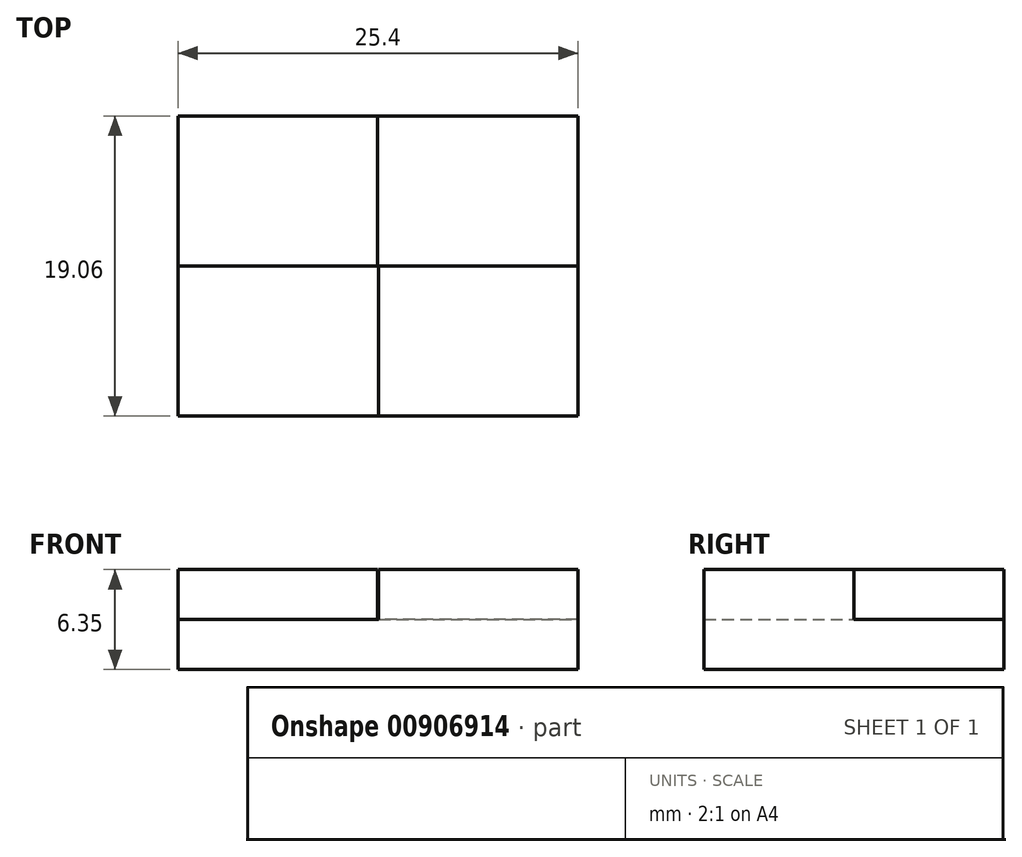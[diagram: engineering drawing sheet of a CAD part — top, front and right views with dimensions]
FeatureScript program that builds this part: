
annotation { "Feature Type Name" : "Feature", "Feature Type Description" : "" }
export const myFeature = defineFeature(function(context is Context, id is Id, definition is map)
    precondition{}
    {
        {
            var Q0;
            Q0=qCreatedBy(makeId("Top.planeOp"),FACE);
            var sketch = newSketch(context, id + "F0", { "sketchPlane" : qUnion([Q0])});
            skLineSegment(sketch, "E0.bottom", {"start": v(12.7, -9.52) * mm, "end": v(-12.7, -9.53) * mm});
            skLineSegment(sketch, "E0.top", {"start": v(12.7, 9.53) * mm, "end": v(-12.7, 9.52) * mm});
            skLineSegment(sketch, "E0.left", {"start": v(12.7, -9.52) * mm, "end": v(12.7, 9.53) * mm});
            skLineSegment(sketch, "E0.right", {"start": v(-12.7, -9.53) * mm, "end": v(-12.7, 9.52) * mm});
            skPoint(sketch, "E0.middle", {"position": v(0, 0) * mm});
            skLineSegment(sketch, "E1", {"start": v(12.7, 0) * mm, "end": v(-12.7, 0) * mm});
            skLineSegment(sketch, "E2", {"start": v(-0.03, 9.53) * mm, "end": v(-0.03, -9.53) * mm});
            skLineSegment(sketch, "E3", {"start": v(0.03, 9.52) * mm, "end": v(0.03, -9.53) * mm});
            skLineSegment(sketch, "E4", {"start": v(0.03, 5.34) * mm, "end": v(0, 5.34) * mm, "construction": true});
            skLineSegment(sketch, "E5", {"start": v(0, 7.47) * mm, "end": v(-0.03, 7.47) * mm, "construction": true});
            skSolve(sketch);
        }
        {
            var Q0;
            {var subQ0=sQuery(id+"F0.wireOp",EDGE,"E0.right");var subQ1=sQuery(id+"F0.wireOp",EDGE,"E0.top");var subQ2=makeQuery(id+"F0.imprint","INTERSECT",VERTEX,{"derivedFrom":[subQ1,subQ0]});Q0=makeQuery(id+"F0.imprint","IMPRINT",FACE,{"disambiguationData":[TD([[makeQuery(id+"F0.imprint","IMPRINT",EDGE,{"disambiguationData":[TD([[subQ2,1.0]])],"derivedFrom":subQ1}),1.0]])]});}
            var Q1;
            {var subQ0=sQuery(id+"F0.wireOp",EDGE,"E0.left");var subQ1=sQuery(id+"F0.wireOp",EDGE,"E0.top");var subQ2=makeQuery(id+"F0.imprint","INTERSECT",VERTEX,{"derivedFrom":[subQ1,subQ0]});Q1=makeQuery(id+"F0.imprint","IMPRINT",FACE,{"disambiguationData":[TD([[makeQuery(id+"F0.imprint","IMPRINT",EDGE,{"disambiguationData":[TD([[subQ2,-1.0]])],"derivedFrom":subQ1}),1.0]])]});}
            var Q2;
            {var subQ0=sQuery(id+"F0.wireOp",EDGE,"E0.left");var subQ1=sQuery(id+"F0.wireOp",EDGE,"E0.bottom");var subQ2=makeQuery(id+"F0.imprint","INTERSECT",VERTEX,{"derivedFrom":[subQ1,subQ0]});Q2=makeQuery(id+"F0.imprint","IMPRINT",FACE,{"disambiguationData":[TD([[makeQuery(id+"F0.imprint","IMPRINT",EDGE,{"disambiguationData":[TD([[subQ2,-1.0]])],"derivedFrom":subQ1}),-1.0]])]});}
            var Q3;
            {var subQ0=sQuery(id+"F0.wireOp",EDGE,"E0.right");var subQ1=sQuery(id+"F0.wireOp",EDGE,"E0.bottom");var subQ2=makeQuery(id+"F0.imprint","INTERSECT",VERTEX,{"derivedFrom":[subQ1,subQ0]});Q3=makeQuery(id+"F0.imprint","IMPRINT",FACE,{"disambiguationData":[TD([[makeQuery(id+"F0.imprint","IMPRINT",EDGE,{"disambiguationData":[TD([[subQ2,1.0]])],"derivedFrom":subQ1}),-1.0]])]});}
            var Q4;
            {var subQ0=sQuery(id+"F0.wireOp",EDGE,"E2");var subQ1=sQuery(id+"F0.wireOp",EDGE,"E0.top");var subQ2=makeQuery(id+"F0.imprint","INTERSECT",VERTEX,{"derivedFrom":[subQ1,subQ0]});Q4=makeQuery(id+"F0.imprint","IMPRINT",FACE,{"disambiguationData":[TD([[makeQuery(id+"F0.imprint","IMPRINT",EDGE,{"disambiguationData":[TD([[subQ2,1.0]])],"derivedFrom":subQ1}),1.0]])]});}
            var Q5;
            {var subQ0=sQuery(id+"F0.wireOp",EDGE,"E2");var subQ1=sQuery(id+"F0.wireOp",EDGE,"E0.bottom");var subQ2=makeQuery(id+"F0.imprint","INTERSECT",VERTEX,{"derivedFrom":[subQ1,subQ0]});Q5=makeQuery(id+"F0.imprint","IMPRINT",FACE,{"disambiguationData":[TD([[makeQuery(id+"F0.imprint","IMPRINT",EDGE,{"disambiguationData":[TD([[subQ2,1.0]])],"derivedFrom":subQ1}),-1.0]])]});}
            extrude(context, id + "F1", {"entities" : qUnion([Q0, Q1, Q2, Q3, Q4, Q5]), "depth" : 3.17 * mm, "offsetDistance" : 25.4 * mm});
        }
        {
            var Q0;
            {var subQ0=sQuery(id+"F0.wireOp",EDGE,"E0.left");var subQ1=sQuery(id+"F0.wireOp",EDGE,"E0.bottom");var subQ2=makeQuery(id+"F0.imprint","INTERSECT",VERTEX,{"derivedFrom":[subQ1,subQ0]});Q0=makeQuery(id+"F0.imprint","IMPRINT",FACE,{"disambiguationData":[TD([[makeQuery(id+"F0.imprint","IMPRINT",EDGE,{"disambiguationData":[TD([[subQ2,-1.0]])],"derivedFrom":subQ1}),-1.0]])]});}
            var Q1;
            {var subQ0=sQuery(id+"F0.wireOp",EDGE,"E0.right");var subQ1=sQuery(id+"F0.wireOp",EDGE,"E0.top");var subQ2=makeQuery(id+"F0.imprint","INTERSECT",VERTEX,{"derivedFrom":[subQ1,subQ0]});Q1=makeQuery(id+"F0.imprint","IMPRINT",FACE,{"disambiguationData":[TD([[makeQuery(id+"F0.imprint","IMPRINT",EDGE,{"disambiguationData":[TD([[subQ2,1.0]])],"derivedFrom":subQ1}),1.0]])]});}
            extrude(context, id + "F2", {"entities" : qUnion([Q0, Q1]), "operationType" : NewBodyOperationType.ADD, "depth" : 6.35 * mm, "offsetDistance" : 25.4 * mm});
        }
    });
